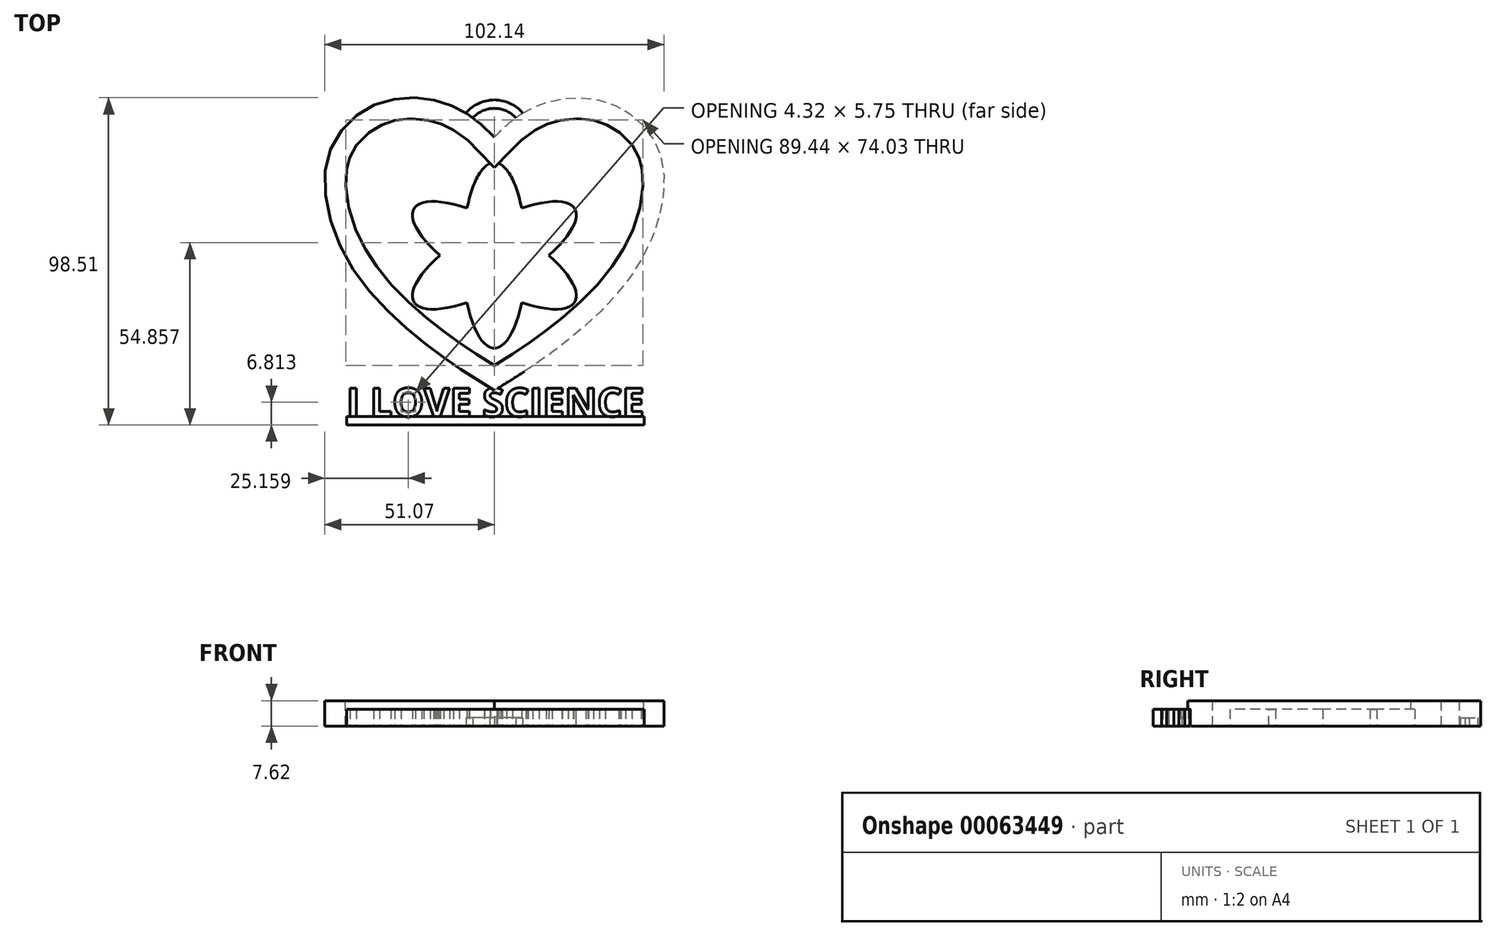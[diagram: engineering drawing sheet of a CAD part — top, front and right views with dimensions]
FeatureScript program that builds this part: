
annotation { "Feature Type Name" : "Feature", "Feature Type Description" : "" }
export const myFeature = defineFeature(function(context is Context, id is Id, definition is map)
    precondition{}
    {
        {
            var Q0;
            Q0=qCreatedBy(makeId("Top.planeOp"),FACE);
            var sketch = newSketch(context, id + "F0", { "sketchPlane" : qUnion([Q0])});
            skLineSegment(sketch, "E0", {"start": v(0, 0) * mm, "end": v(0, -76.2) * mm, "construction": true});
            skFitSpline(sketch, "E1", {"points": [v(0, 0) * mm, v(-13.73, 9.83) * mm, v(-33.82, 10.56) * mm, v(-49.92, -5.3) * mm, v(-43.74, -37.74) * mm, v(-18.85, -63.6) * mm, v(0, -76.2) * mm], "startDerivative": vector(-94.95, 99.8) * mm, "endDerivative": vector(120.56, -72.9) * mm});
            skFitSpline(sketch, "E2.0", {"points": [v(-4.6, -4.38) * mm, v(-5.52, -3.41) * mm, v(-7.28, -1.66) * mm, v(-9.76, 0.46) * mm, v(-11.8, 1.86) * mm, v(-13.49, 2.8) * mm, v(-14.81, 3.44) * mm, v(-16.22, 4) * mm, v(-17.74, 4.5) * mm, v(-19.33, 4.91) * mm, v(-21.55, 5.34) * mm, v(-24.41, 5.62) * mm, v(-27.3, 5.5) * mm, v(-29.54, 5.15) * mm, v(-31.18, 4.75) * mm, v(-32.76, 4.23) * mm, v(-34.32, 3.55) * mm, v(-35.83, 2.73) * mm, v(-37.76, 1.47) * mm, v(-39.93, -0.42) * mm, v(-41.7, -2.65) * mm, v(-42.84, -4.61) * mm, v(-43.42, -5.9) * mm, v(-43.8, -6.99) * mm, v(-44.13, -8.1) * mm, v(-44.46, -9.6) * mm, v(-44.68, -11.53) * mm, v(-44.77, -14.29) * mm, v(-44.47, -18.02) * mm, v(-43.44, -22.77) * mm, v(-41.79, -27.61) * mm, v(-39.94, -31.59) * mm, v(-38.22, -34.64) * mm, v(-36.34, -37.62) * mm, v(-33.7, -41.2) * mm, v(-30.17, -45.26) * mm, v(-26.39, -49.07) * mm, v(-22.45, -52.62) * mm, v(-19.15, -55.34) * mm, v(-16.54, -57.38) * mm, v(-13.98, -59.33) * mm, v(-10.9, -61.57) * mm, v(-7.37, -64.03) * mm, v(-3.88, -66.32) * mm, v(-0.37, -68.54) * mm, v(2.05, -70.02) * mm, v(3.29, -70.77) * mm]});
            skLineSegment(sketch, "E3", {"start": v(0, -76.2) * mm, "end": v(0, -68.76) * mm});
            skLineSegment(sketch, "E4", {"start": v(-4.89, -4.08) * mm, "end": v(0, -9.16) * mm});
            skLineSegment(sketch, "E5", {"start": v(0, -9.16) * mm, "end": v(0, 0) * mm});
            skSolve(sketch);
        }
        {
            var Q0;
            Q0 = qSketchRegion(id + "F0", true);
            extrude(context, id + "F1", {"entities" : qUnion([Q0]), "depth" : 7.62 * mm});
        }
        {
            var Q0;
            Q0=makeQuery(id+"F1.opExtrude","SWEPT_BODY",BODY,{"disambiguationData":[OSD([sQuery(id+"F0.wireOp",EDGE,"E1"),sQuery(id+"F0.wireOp",EDGE,"E2.0"),sQuery(id+"F0.wireOp",EDGE,"E3"),sQuery(id+"F0.wireOp",EDGE,"E4"),sQuery(id+"F0.wireOp",EDGE,"E5")])]});
            var Q1;
            Q1=qCreatedBy(makeId("Right.planeOp"),FACE);
            mirror(context, id + "F2", {"operationType" : NewBodyOperationType.ADD, "entities" : qUnion([Q0]), "mirrorPlane" : qUnion([Q1])});
        }
        {
            var Q0;
            Q0=qCreatedBy(makeId("Top.planeOp"),FACE);
            var sketch = newSketch(context, id + "F3", { "sketchPlane" : qUnion([Q0])});
            skEllipse(sketch, "E6", {"center": v(0, -35.56) * mm, "majorRadius": 27.94 * mm, "minorRadius": 9.53 * mm, "majorAxis": v(0, -1)});
            skFitSpline(sketch, "E7.0", {"points": [v(-0.84, -66) * mm, v(0, -66.06) * mm, v(0.84, -66) * mm, v(1.93, -65.76) * mm, v(3.19, -65.2) * mm, v(4.49, -64.23) * mm, v(5.63, -63.02) * mm, v(6.64, -61.6) * mm, v(7.56, -60) * mm, v(8.26, -58.48) * mm, v(8.77, -57.18) * mm, v(9.14, -56.14) * mm, v(9.5, -55.07) * mm, v(9.93, -53.59) * mm, v(10.42, -51.65) * mm, v(10.92, -49.19) * mm, v(11.33, -46.62) * mm, v(11.65, -43.96) * mm, v(11.89, -41.22) * mm, v(12, -38.88) * mm, v(12.06, -37) * mm, v(12.07, -35.56) * mm, v(12.06, -34.13) * mm, v(12, -32.24) * mm, v(11.89, -29.9) * mm, v(11.65, -27.16) * mm, v(11.33, -24.5) * mm, v(10.92, -21.93) * mm, v(10.42, -19.47) * mm, v(9.93, -17.53) * mm, v(9.5, -16.05) * mm, v(9.14, -14.98) * mm, v(8.77, -13.94) * mm, v(8.26, -12.64) * mm, v(7.56, -11.12) * mm, v(6.64, -9.51) * mm, v(5.63, -8.1) * mm, v(4.49, -6.9) * mm, v(3.19, -5.92) * mm, v(1.93, -5.36) * mm, v(0.84, -5.12) * mm, v(0, -5.06) * mm, v(-0.84, -5.12) * mm, v(-1.93, -5.36) * mm, v(-3.19, -5.92) * mm, v(-4.49, -6.9) * mm, v(-5.63, -8.1) * mm, v(-6.64, -9.51) * mm, v(-7.56, -11.12) * mm, v(-8.26, -12.64) * mm, v(-8.77, -13.94) * mm, v(-9.14, -14.98) * mm, v(-9.5, -16.05) * mm, v(-9.93, -17.53) * mm, v(-10.42, -19.47) * mm, v(-10.92, -21.93) * mm, v(-11.33, -24.5) * mm, v(-11.65, -27.16) * mm, v(-11.89, -29.9) * mm, v(-12, -32.24) * mm, v(-12.06, -34.13) * mm, v(-12.07, -35.56) * mm, v(-12.06, -37) * mm, v(-12, -38.88) * mm, v(-11.89, -41.22) * mm, v(-11.65, -43.96) * mm, v(-11.33, -46.62) * mm, v(-10.92, -49.19) * mm, v(-10.42, -51.65) * mm, v(-9.93, -53.59) * mm, v(-9.5, -55.07) * mm, v(-9.14, -56.14) * mm, v(-8.77, -57.18) * mm, v(-8.26, -58.48) * mm, v(-7.56, -60) * mm, v(-6.64, -61.6) * mm, v(-5.63, -63.02) * mm, v(-4.49, -64.23) * mm, v(-3.19, -65.2) * mm, v(-1.93, -65.76) * mm, v(-0.84, -66) * mm, v(0, -66.06) * mm, v(0.84, -66) * mm, v(-0.84, -66) * mm]});
            skSolve(sketch);
        }
        {
            var Q0;
            Q0 = qSketchRegion(id + "F3", true);
            extrude(context, id + "F4", {"entities" : qUnion([Q0]), "depth" : 5.08 * mm});
        }
        {
            var Q0;
            Q0=qCreatedBy(makeId("Right.planeOp"),FACE);
            var sketch = newSketch(context, id + "F5", { "sketchPlane" : qUnion([Q0])});
            skLineSegment(sketch, "E8", {"start": v(-35.56, 0) * mm, "end": v(-35.56, 31.4) * mm});
            skSolve(sketch);
        }
        {
            var Q0;
            Q0=makeQuery(id+"F4.opExtrude","SWEPT_BODY",BODY,{"disambiguationData":[OSD([sQuery(id+"F3.wireOp",EDGE,"E6"),sQuery(id+"F3.wireOp",EDGE,"E7.0")])]});
            var Q1;
            Q1=sQuery(id+"F5.wireOp",EDGE,"E8");
            circularPattern(context, id + "F6", {"operationType" : NewBodyOperationType.ADD, "entities" : qUnion([Q0]), "axis" : qUnion([Q1]), "angle" : 120 * degree, "instanceCount" : 3});
        }
        {
            var Q0;
            Q0=qCreatedBy(makeId("Top.planeOp"),FACE);
            var sketch = newSketch(context, id + "F7", { "sketchPlane" : qUnion([Q0])});
            skText(sketch, "E9", { "text": "I LOVE SCIENCE", "fontName": "OpenSans-Bold.ttf"});
            const initialGuessF7  = {"E9": [-0.04445, -0.08407, 1, 0, 0.00859]};
            skSetInitialGuess(sketch, initialGuessF7);
            skSolve(sketch);
        }
        {
            var Q0;
            Q0 = qSketchRegion(id + "F7", true);
            extrude(context, id + "F8", {"entities" : qUnion([Q0]), "operationType" : NewBodyOperationType.ADD, "depth" : 5.08 * mm});
        }
        {
            var Q0;
            Q0=qCreatedBy(makeId("Top.planeOp"),FACE);
            var sketch = newSketch(context, id + "F9", { "sketchPlane" : qUnion([Q0])});
            skLineSegment(sketch, "E10.bottom", {"start": v(-44.45, -84.07) * mm, "end": v(45.09, -84.07) * mm});
            skLineSegment(sketch, "E10.top", {"start": v(-44.45, -86.61) * mm, "end": v(45.09, -86.61) * mm});
            skLineSegment(sketch, "E10.left", {"start": v(-44.45, -84.07) * mm, "end": v(-44.45, -86.61) * mm});
            skLineSegment(sketch, "E10.right", {"start": v(45.09, -84.07) * mm, "end": v(45.09, -86.61) * mm});
            skSolve(sketch);
        }
        {
            var Q0;
            Q0 = qSketchRegion(id + "F9", true);
            extrude(context, id + "F10", {"entities" : qUnion([Q0]), "depth" : 5.08 * mm});
        }
        {
            var Q0;
            Q0=qCreatedBy(makeId("Right.planeOp"),FACE);
            var sketch = newSketch(context, id + "F11", { "sketchPlane" : qUnion([Q0])});
            skLineSegment(sketch, "E11.bottom", {"start": v(8.7, 0) * mm, "end": v(11.25, 0) * mm});
            skLineSegment(sketch, "E11.top", {"start": v(8.7, 2.54) * mm, "end": v(11.25, 2.54) * mm});
            skLineSegment(sketch, "E11.left", {"start": v(8.7, 0) * mm, "end": v(8.7, 2.54) * mm});
            skLineSegment(sketch, "E11.right", {"start": v(11.25, 0) * mm, "end": v(11.25, 2.54) * mm});
            skSolve(sketch);
        }
        {
            var Q0;
            Q0=makeQuery(id+"F11.imprint","IMPRINT",FACE,{"disambiguationData":[TD([[makeQuery(id+"F11.imprint","IMPRINT",EDGE,{"derivedFrom":sQuery(id+"F11.wireOp",EDGE,"E11.bottom")}),1.0]])]});
            var Q1;
            {var subQ0=makeQuery(id+"F1.opExtrude","SWEPT_EDGE",EDGE,{"disambiguationData":[OSD([sQuery(id+"F0.wireOp",EDGE,"E1"),sQuery(id+"F0.wireOp",EDGE,"E5")])]});Q1=makeQuery(id+"F2.boolean.opBoolean","MERGE",EDGE,{"derivedFrom":[subQ0,makeQuery(id+"F2.opPattern","COPY",EDGE,{"derivedFrom":subQ0,"instanceName":"1"})]});}
            revolve(context, id + "F12", {"operationType" : NewBodyOperationType.ADD, "entities" : qUnion([Q0]), "axis" : qUnion([Q1]), "revolveType" : RevolveType.SYMMETRIC, "angle" : 111.86 * degree});
        }
    });
